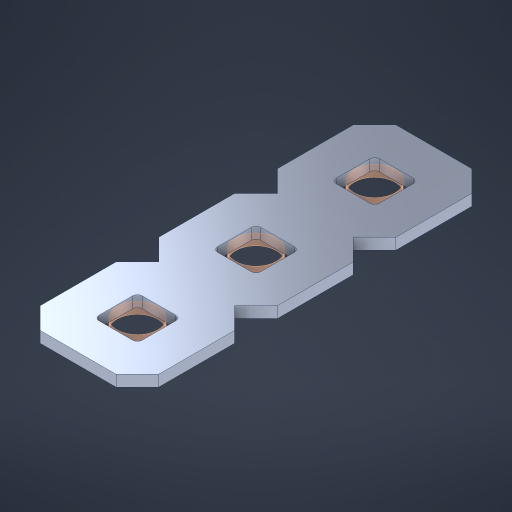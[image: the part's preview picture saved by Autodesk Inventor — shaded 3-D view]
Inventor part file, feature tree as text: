
AUTODESK INVENTOR PART (.ipt)
format: ipt  version: 2023 (Build 270158000, 158)  size: 297,984 bytes
history: native  units: in
note: dims shown in document units (in); Inventor stores cm internally (conversion verified against a paired STEP export)
features: other x4, sketch x2, extrude x2, pattern_linear x1
ambient origin geometry x8: Origin, YZ Plane, XZ Plane, XY Plane, X Axis, Y Axis, Z Axis, Center Point
bodies: Solid1 (feature_tree), Body (feature_tree)
feature tree (9):
  pattern_linear  "Rectangular Pattern1"  Spacing1=0.09in  [1 undecoded]
  sketch  "Sketch1"  dims[d1=0.5in]
  sketch  "Sketch2"  dims[d2=0.182in d3=0.09in d4=0.09in d5=0.09in d6=0.09in d7=0.09in d8=0.09in d9=0.09in d10=0.09in d11=0.02in d13=0.0in d14=0.172in d15=0.0625in d16=0.0in d19=0.5in d22=0.5in]
  other  "Srf1"
  other  "Srf126"
  other  "Srf127"
  other  "Circle"
  extrude  "ExtrusionSrf126"  Depth=0.09in
  extrude  "ExtrusionSrf127"  Depth=0.09in
note: 1 required parameter value undecoded (feature->parameter linkage not recoverable at this tier; creation-order binding heuristic only, values carry confidence <= 0.55)
